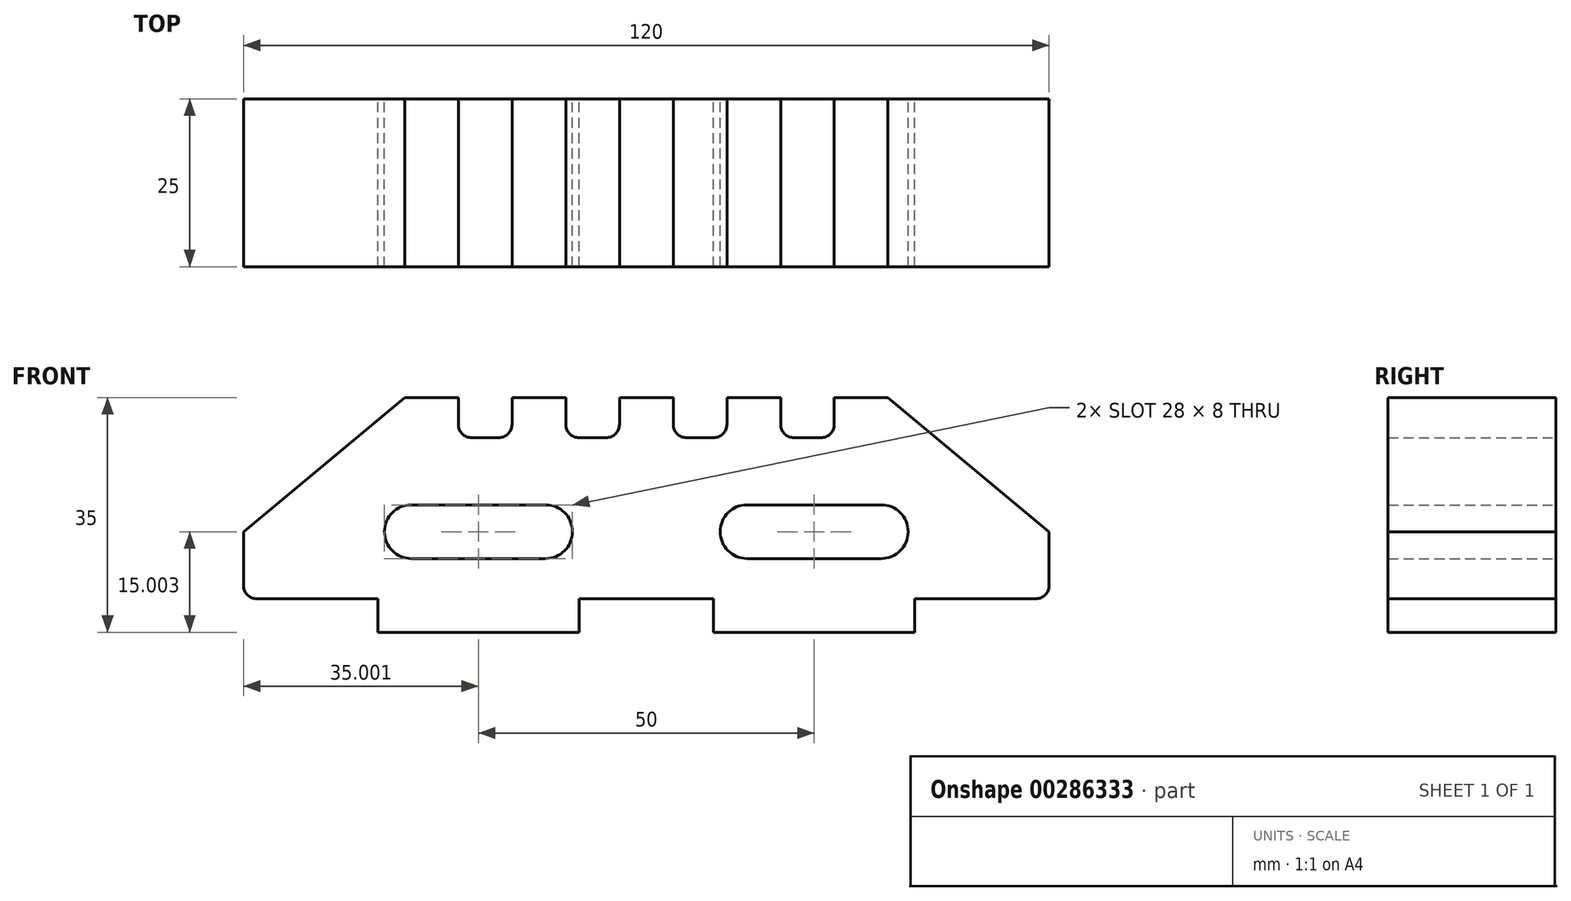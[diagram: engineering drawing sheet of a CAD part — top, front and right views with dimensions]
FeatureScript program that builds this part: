
annotation { "Feature Type Name" : "Feature", "Feature Type Description" : "" }
export const myFeature = defineFeature(function(context is Context, id is Id, definition is map)
    precondition{}
    {
        {
            var Q0;
            Q0=qCreatedBy(makeId("Front.planeOp"),FACE);
            var sketch = newSketch(context, id + "F0", { "sketchPlane" : qUnion([Q0])});
            skLineSegment(sketch, "E0", {"start": v(-223.47, -64.04) * mm, "end": v(-205.47, -64.04) * mm});
            skLineSegment(sketch, "E1", {"start": v(-205.47, -64.04) * mm, "end": v(-205.47, -69.04) * mm});
            skLineSegment(sketch, "E2", {"start": v(-205.47, -69.04) * mm, "end": v(-175.47, -69.04) * mm});
            skLineSegment(sketch, "E3", {"start": v(-175.47, -69.04) * mm, "end": v(-175.47, -64.04) * mm});
            skLineSegment(sketch, "E4", {"start": v(-175.47, -64.04) * mm, "end": v(-155.47, -64.04) * mm});
            skLineSegment(sketch, "E5", {"start": v(-155.47, -64.04) * mm, "end": v(-155.47, -69.04) * mm});
            skLineSegment(sketch, "E6", {"start": v(-155.47, -69.04) * mm, "end": v(-125.47, -69.04) * mm});
            skLineSegment(sketch, "E7", {"start": v(-125.47, -69.04) * mm, "end": v(-125.47, -64.04) * mm});
            skLineSegment(sketch, "E8", {"start": v(-125.47, -64.04) * mm, "end": v(-107.47, -64.04) * mm});
            skLineSegment(sketch, "E9", {"start": v(-105.47, -62.04) * mm, "end": v(-105.47, -54.04) * mm});
            skLineSegment(sketch, "E10", {"start": v(-225.47, -62.04) * mm, "end": v(-225.47, -54.04) * mm});
            skLineSegment(sketch, "E11", {"start": v(-201.47, -34.04) * mm, "end": v(-225.47, -54.04) * mm});
            skLineSegment(sketch, "E12", {"start": v(-129.47, -34.04) * mm, "end": v(-105.47, -54.04) * mm});
            skLineSegment(sketch, "E13", {"start": v(-129.47, -34.04) * mm, "end": v(-137.47, -34.04) * mm});
            skLineSegment(sketch, "E14", {"start": v(-137.47, -34.04) * mm, "end": v(-137.47, -38.04) * mm});
            skLineSegment(sketch, "E15", {"start": v(-139.47, -40.04) * mm, "end": v(-143.47, -40.04) * mm});
            skLineSegment(sketch, "E16", {"start": v(-145.47, -38.04) * mm, "end": v(-145.47, -34.04) * mm});
            skLineSegment(sketch, "E17", {"start": v(-145.47, -34.04) * mm, "end": v(-153.47, -34.04) * mm});
            skLineSegment(sketch, "E18", {"start": v(-153.47, -34.04) * mm, "end": v(-153.47, -38.04) * mm});
            skLineSegment(sketch, "E19", {"start": v(-155.47, -40.04) * mm, "end": v(-159.47, -40.04) * mm});
            skLineSegment(sketch, "E20", {"start": v(-161.47, -38.04) * mm, "end": v(-161.47, -34.04) * mm});
            skLineSegment(sketch, "E21", {"start": v(-161.47, -34.04) * mm, "end": v(-169.47, -34.04) * mm});
            skLineSegment(sketch, "E22", {"start": v(-169.47, -34.04) * mm, "end": v(-169.47, -38.04) * mm});
            skLineSegment(sketch, "E23", {"start": v(-171.47, -40.04) * mm, "end": v(-175.47, -40.04) * mm});
            skLineSegment(sketch, "E24", {"start": v(-177.47, -38.04) * mm, "end": v(-177.47, -34.04) * mm});
            skLineSegment(sketch, "E25", {"start": v(-177.47, -34.04) * mm, "end": v(-185.47, -34.04) * mm});
            skLineSegment(sketch, "E26", {"start": v(-185.47, -34.04) * mm, "end": v(-185.47, -38.04) * mm});
            skLineSegment(sketch, "E27", {"start": v(-187.47, -40.04) * mm, "end": v(-191.47, -40.04) * mm});
            skLineSegment(sketch, "E28", {"start": v(-193.47, -38.04) * mm, "end": v(-193.47, -34.04) * mm});
            skLineSegment(sketch, "E29", {"start": v(-193.47, -34.04) * mm, "end": v(-201.47, -34.04) * mm});
            skLineSegment(sketch, "E30", {"start": v(-175.47, -64.04) * mm, "end": v(-165.47, -64.04) * mm});
            skLineSegment(sketch, "E31", {"start": v(-165.47, -64.04) * mm, "end": v(-165.47, -34.04) * mm});
            skPoint(sketch, "E31.endSnap0", {"position": v(-165.47, -34.04) * mm});
            skLineSegment(sketch, "E32", {"start": v(-140.47, -69.04) * mm, "end": v(-140.47, -54.04) * mm});
            skLineSegment(sketch, "E33", {"start": v(-140.47, -54.04) * mm, "end": v(-165.47, -54.04) * mm});
            skLineSegment(sketch, "E34", {"start": v(-165.47, -54.04) * mm, "end": v(-154.47, -54.04) * mm});
            skLineSegment(sketch, "E35", {"start": v(-154.47, -54.04) * mm, "end": v(-154.47, -54.04) * mm});
            skLineSegment(sketch, "E36", {"start": v(-150.47, -58.04) * mm, "end": v(-130.47, -58.04) * mm});
            skLineSegment(sketch, "E37", {"start": v(-126.47, -54.04) * mm, "end": v(-126.47, -54.04) * mm});
            skLineSegment(sketch, "E38", {"start": v(-130.47, -50.04) * mm, "end": v(-150.47, -50.04) * mm});
            skLineSegment(sketch, "E39", {"start": v(-165.47, -54.04) * mm, "end": v(-189.83, -54.04) * mm});
            skLineSegment(sketch, "E40", {"start": v(-165.47, -54.04) * mm, "end": v(-176.47, -54.04) * mm});
            skLineSegment(sketch, "E41", {"start": v(-176.47, -54.04) * mm, "end": v(-176.47, -54.04) * mm});
            skLineSegment(sketch, "E42", {"start": v(-180.47, -58.04) * mm, "end": v(-200.47, -58.04) * mm});
            skLineSegment(sketch, "E43", {"start": v(-204.47, -54.04) * mm, "end": v(-204.47, -54.04) * mm});
            skLineSegment(sketch, "E44", {"start": v(-200.47, -50.04) * mm, "end": v(-180.47, -50.04) * mm});
            skPoint(sketch, "E45.visualSharp", {"position": v(-137.47, -40.04) * mm});
            skArc(sketch, "E45.filletArc", {"start": v(-139.47, -40.04) * mm, "mid": v(-138.05, -39.45) * mm, "end": v(-137.47, -38.04) * mm});
            skPoint(sketch, "E46.visualSharp", {"position": v(-145.47, -40.04) * mm});
            skArc(sketch, "E46.filletArc", {"start": v(-145.47, -38.04) * mm, "mid": v(-144.88, -39.45) * mm, "end": v(-143.47, -40.04) * mm});
            skPoint(sketch, "E47.visualSharp", {"position": v(-153.47, -40.04) * mm});
            skArc(sketch, "E47.filletArc", {"start": v(-155.47, -40.04) * mm, "mid": v(-154.05, -39.45) * mm, "end": v(-153.47, -38.04) * mm});
            skPoint(sketch, "E48.visualSharp", {"position": v(-161.47, -40.04) * mm});
            skArc(sketch, "E48.filletArc", {"start": v(-161.47, -38.04) * mm, "mid": v(-160.88, -39.45) * mm, "end": v(-159.47, -40.04) * mm});
            skPoint(sketch, "E49.visualSharp", {"position": v(-169.47, -40.04) * mm});
            skArc(sketch, "E49.filletArc", {"start": v(-171.47, -40.04) * mm, "mid": v(-170.05, -39.45) * mm, "end": v(-169.47, -38.04) * mm});
            skPoint(sketch, "E50.visualSharp", {"position": v(-177.47, -40.04) * mm});
            skArc(sketch, "E50.filletArc", {"start": v(-177.47, -38.04) * mm, "mid": v(-176.88, -39.45) * mm, "end": v(-175.47, -40.04) * mm});
            skPoint(sketch, "E51.visualSharp", {"position": v(-185.47, -40.04) * mm});
            skArc(sketch, "E51.filletArc", {"start": v(-187.47, -40.04) * mm, "mid": v(-186.05, -39.45) * mm, "end": v(-185.47, -38.04) * mm});
            skPoint(sketch, "E52.visualSharp", {"position": v(-193.47, -40.04) * mm});
            skArc(sketch, "E52.filletArc", {"start": v(-193.47, -38.04) * mm, "mid": v(-192.88, -39.45) * mm, "end": v(-191.47, -40.04) * mm});
            skLineSegment(sketch, "E53", {"start": v(-140.47, -54.04) * mm, "end": v(-126.47, -54.04) * mm});
            skPoint(sketch, "E54.visualSharp", {"position": v(-126.47, -58.04) * mm});
            skArc(sketch, "E54.filletArc", {"start": v(-130.47, -58.04) * mm, "mid": v(-127.64, -56.87) * mm, "end": v(-126.47, -54.04) * mm});
            skPoint(sketch, "E55.visualSharp", {"position": v(-126.47, -50.04) * mm});
            skArc(sketch, "E55.filletArc", {"start": v(-126.47, -54.04) * mm, "mid": v(-127.64, -51.2) * mm, "end": v(-130.47, -50.04) * mm});
            skPoint(sketch, "E56.visualSharp", {"position": v(-154.47, -50.04) * mm});
            skArc(sketch, "E56.filletArc", {"start": v(-150.47, -50.04) * mm, "mid": v(-153.3, -51.2) * mm, "end": v(-154.47, -54.04) * mm});
            skPoint(sketch, "E57.visualSharp", {"position": v(-154.47, -58.04) * mm});
            skArc(sketch, "E57.filletArc", {"start": v(-154.47, -54.04) * mm, "mid": v(-153.3, -56.87) * mm, "end": v(-150.47, -58.04) * mm});
            skPoint(sketch, "E58.visualSharp", {"position": v(-176.47, -58.04) * mm});
            skArc(sketch, "E58.filletArc", {"start": v(-180.47, -58.04) * mm, "mid": v(-177.64, -56.87) * mm, "end": v(-176.47, -54.04) * mm});
            skPoint(sketch, "E59.visualSharp", {"position": v(-176.47, -50.04) * mm});
            skArc(sketch, "E59.filletArc", {"start": v(-176.47, -54.04) * mm, "mid": v(-177.64, -51.2) * mm, "end": v(-180.47, -50.04) * mm});
            skPoint(sketch, "E60.visualSharp", {"position": v(-204.47, -50.04) * mm});
            skArc(sketch, "E60.filletArc", {"start": v(-200.47, -50.04) * mm, "mid": v(-203.3, -51.2) * mm, "end": v(-204.47, -54.04) * mm});
            skPoint(sketch, "E61.visualSharp", {"position": v(-204.47, -58.04) * mm});
            skArc(sketch, "E61.filletArc", {"start": v(-204.47, -54.04) * mm, "mid": v(-203.3, -56.87) * mm, "end": v(-200.47, -58.04) * mm});
            skPoint(sketch, "E62.orphan", {"position": v(-165.47, -7.3) * mm});
            skPoint(sketch, "E63.visualSharp", {"position": v(-105.47, -64.04) * mm});
            skArc(sketch, "E63.filletArc", {"start": v(-107.47, -64.04) * mm, "mid": v(-106.05, -63.45) * mm, "end": v(-105.47, -62.04) * mm});
            skPoint(sketch, "E64.visualSharp", {"position": v(-225.47, -64.04) * mm});
            skArc(sketch, "E64.filletArc", {"start": v(-225.47, -62.04) * mm, "mid": v(-224.88, -63.45) * mm, "end": v(-223.47, -64.04) * mm});
            skSolve(sketch);
        }
        {
            var Q0;
            Q0=makeQuery(id+"F0.imprint","IMPRINT",FACE,{"disambiguationData":[TD([[makeQuery(id+"F0.imprint","IMPRINT",EDGE,{"derivedFrom":sQuery(id+"F0.wireOp",EDGE,"E0")}),1.0]])]});
            var Q1;
            {var subQ10=sQuery(id+"F0.wireOp",EDGE,"E7");Q1=makeQuery(id+"F0.imprint","IMPRINT",FACE,{"disambiguationData":[TD([[makeQuery(id+"F0.imprint","IMPRINT",EDGE,{"derivedFrom":subQ10}),1.0]])]});}
            var Q2;
            {var subQ1=sQuery(id+"F0.wireOp",EDGE,"E4");Q2=makeQuery(id+"F0.imprint","IMPRINT",FACE,{"disambiguationData":[TD([[makeQuery(id+"F0.imprint","IMPRINT",EDGE,{"derivedFrom":subQ1}),1.0]])]});}
            extrude(context, id + "F1", {"entities" : qUnion([Q0, Q1, Q2]), "depth" : 25 * mm});
        }
    });
